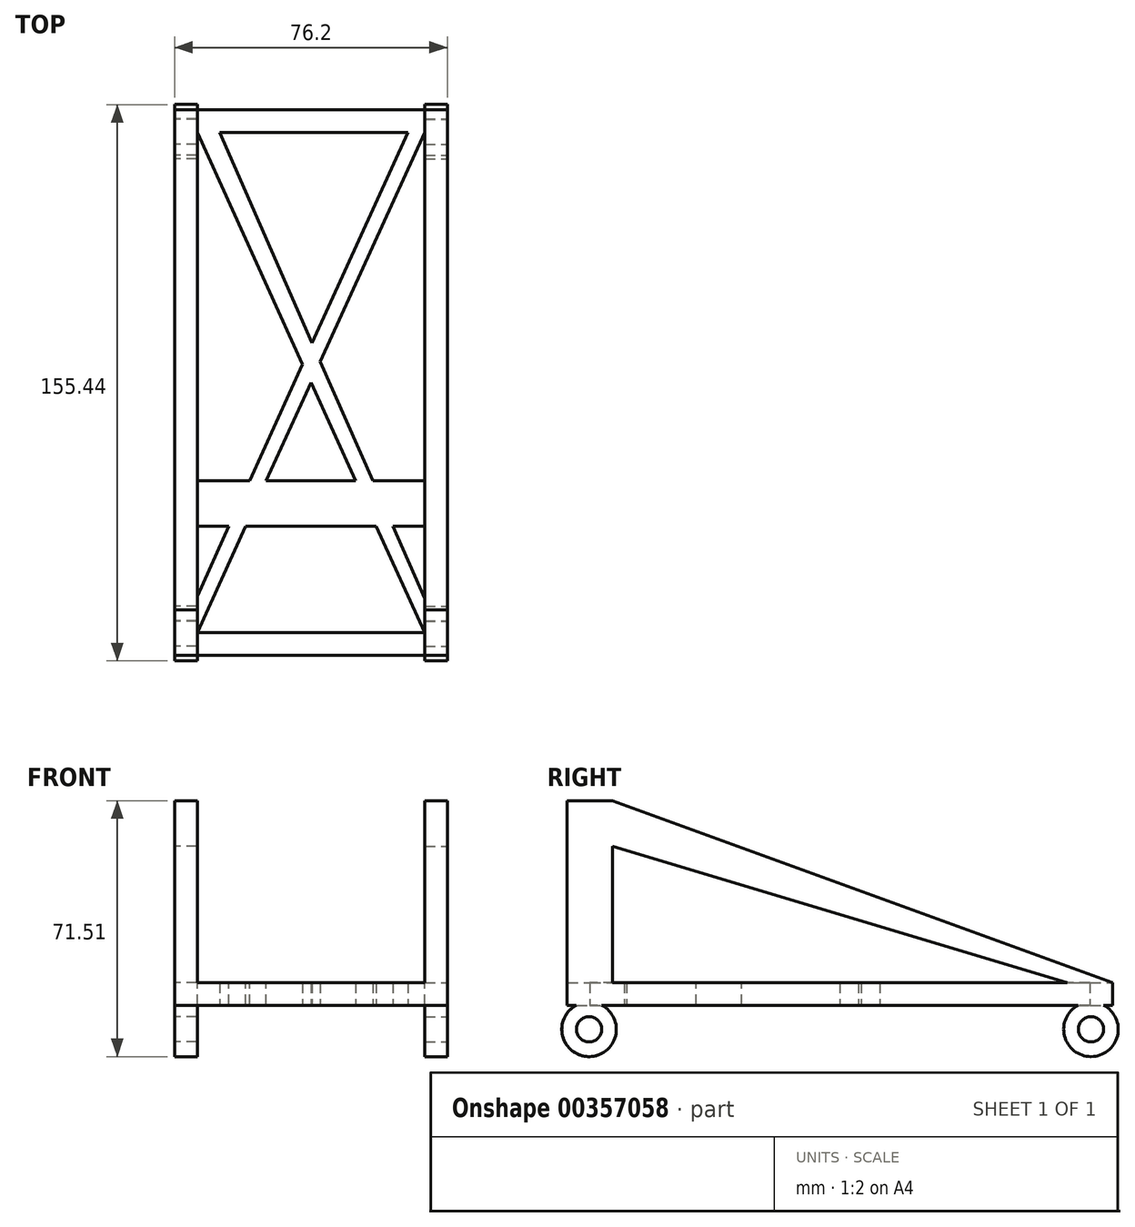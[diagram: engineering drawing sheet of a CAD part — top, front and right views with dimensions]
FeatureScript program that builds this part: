
annotation { "Feature Type Name" : "Feature", "Feature Type Description" : "" }
export const myFeature = defineFeature(function(context is Context, id is Id, definition is map)
    precondition{}
    {
        {
            var Q0;
            Q0=qCreatedBy(makeId("Top.planeOp"),FACE);
            var sketch = newSketch(context, id + "F0", { "sketchPlane" : qUnion([Q0])});
            skLineSegment(sketch, "E0.bottom", {"start": v(-38.1, -76.2) * mm, "end": v(38.1, -76.2) * mm});
            skLineSegment(sketch, "E0.top", {"start": v(-38.1, 76.2) * mm, "end": v(38.1, 76.2) * mm});
            skLineSegment(sketch, "E0.left", {"start": v(-38.1, -76.2) * mm, "end": v(-38.1, 76.2) * mm});
            skLineSegment(sketch, "E0.right", {"start": v(38.1, -76.2) * mm, "end": v(38.1, 76.2) * mm});
            skPoint(sketch, "E0.middle", {"position": v(0, 0) * mm});
            skLineSegment(sketch, "E1.bottom", {"start": v(-31.75, 69.85) * mm, "end": v(31.75, 69.85) * mm});
            skLineSegment(sketch, "E1.top", {"start": v(-31.75, -69.85) * mm, "end": v(31.75, -69.85) * mm});
            skLineSegment(sketch, "E1.left", {"start": v(-31.75, 69.85) * mm, "end": v(-31.75, -69.85) * mm});
            skLineSegment(sketch, "E1.right", {"start": v(31.75, 69.85) * mm, "end": v(31.75, -69.85) * mm});
            skLineSegment(sketch, "E2", {"start": v(-31.75, -59.6) * mm, "end": v(27.09, 69.85) * mm});
            skLineSegment(sketch, "E3", {"start": v(-31.75, -69.85) * mm, "end": v(31.75, 69.85) * mm});
            skLineSegment(sketch, "E4", {"start": v(-25.47, 69.85) * mm, "end": v(31.75, -60.32) * mm});
            skLineSegment(sketch, "E5", {"start": v(-31.75, 69.85) * mm, "end": v(31.75, -69.85) * mm});
            skSolve(sketch);
        }
        {
            var Q0;
            Q0=qSketchRegion(id+"F0",true);
            var Q1;
            {var subQ0=sQuery(id+"F0.wireOp",EDGE,"E5");var subQ5=sQuery(id+"F0.wireOp",EDGE,"E2");var subQ6=makeQuery(id+"F0.imprint","INTERSECT",VERTEX,{"derivedFrom":[subQ5,subQ0]});Q1=makeQuery(id+"F0.imprint","IMPRINT",FACE,{"disambiguationData":[TD([[makeQuery(id+"F0.imprint","IMPRINT",EDGE,{"disambiguationData":[TD([[subQ6,-1.0]])],"derivedFrom":subQ5}),1.0]])]});}
            var Q2;
            {var subQ1=sQuery(id+"F0.wireOp",EDGE,"E1.bottom");var subQ3=sQuery(id+"F0.wireOp",EDGE,"E2");var subQ4=makeQuery(id+"F0.imprint","INTERSECT",VERTEX,{"derivedFrom":[subQ1,subQ3]});Q2=makeQuery(id+"F0.imprint","IMPRINT",FACE,{"disambiguationData":[TD([[makeQuery(id+"F0.imprint","IMPRINT",EDGE,{"disambiguationData":[TD([[subQ4,1.0]])],"derivedFrom":subQ3}),-1.0]])]});}
            var Q3;
            {var subQ0=sQuery(id+"F0.wireOp",EDGE,"E5");var subQ5=sQuery(id+"F0.wireOp",EDGE,"E3");var subQ6=makeQuery(id+"F0.imprint","INTERSECT",VERTEX,{"derivedFrom":[subQ5,subQ0]});Q3=makeQuery(id+"F0.imprint","IMPRINT",FACE,{"disambiguationData":[TD([[makeQuery(id+"F0.imprint","IMPRINT",EDGE,{"disambiguationData":[TD([[subQ6,-1.0]])],"derivedFrom":subQ5}),-1.0]])]});}
            var Q4;
            {var subQ1=sQuery(id+"F0.wireOp",EDGE,"E1.left");var subQ3=sQuery(id+"F0.wireOp",EDGE,"E2");var subQ4=makeQuery(id+"F0.imprint","INTERSECT",VERTEX,{"derivedFrom":[subQ1,subQ3]});Q4=makeQuery(id+"F0.imprint","IMPRINT",FACE,{"disambiguationData":[TD([[makeQuery(id+"F0.imprint","IMPRINT",EDGE,{"disambiguationData":[TD([[subQ4,-1.0]])],"derivedFrom":subQ3}),-1.0]])]});}
            var Q5;
            {var subQ0=sQuery(id+"F0.wireOp",EDGE,"E5");var subQ1=sQuery(id+"F0.wireOp",EDGE,"E2");var subQ2=makeQuery(id+"F0.imprint","INTERSECT",VERTEX,{"derivedFrom":[subQ1,subQ0]});Q5=makeQuery(id+"F0.imprint","IMPRINT",FACE,{"disambiguationData":[TD([[makeQuery(id+"F0.imprint","IMPRINT",EDGE,{"disambiguationData":[TD([[subQ2,-1.0]])],"derivedFrom":subQ1}),-1.0]])]});}
            extrude(context, id + "F1", {"entities" : qUnion([Q0, Q1, Q2, Q3, Q4, Q5]), "endBound" : BoundingType.SYMMETRIC, "depth" : 6.35 * mm});
        }
        {
            var Q0;
            Q0=makeQuery(id+"F1.opExtrude","SWEPT_FACE",FACE,{"disambiguationData":[OSD([sQuery(id+"F0.wireOp",EDGE,"E0.right")])]});
            var sketch = newSketch(context, id + "F2", { "sketchPlane" : qUnion([Q0])});
            skLineSegment(sketch, "E6.bottom", {"start": v(-76.2, 3.18) * mm, "end": v(-63.5, 3.18) * mm});
            skLineSegment(sketch, "E6.top", {"start": v(-76.2, 53.98) * mm, "end": v(-63.5, 53.98) * mm});
            skLineSegment(sketch, "E6.left", {"start": v(-76.2, 3.17) * mm, "end": v(-76.2, 53.98) * mm});
            skLineSegment(sketch, "E6.right", {"start": v(-63.5, 3.17) * mm, "end": v(-63.5, 53.98) * mm});
            skLineSegment(sketch, "E7", {"start": v(-63.5, 53.98) * mm, "end": v(76.2, 3.17) * mm});
            skLineSegment(sketch, "E8", {"start": v(-63.5, 41.27) * mm, "end": v(63.5, 3.18) * mm});
            skSolve(sketch);
        }
        {
            var Q0;
            Q0=qSketchRegion(id+"F2",true);
            var Q1;
            {var subQ0=sQuery(id+"F2.wireOp",EDGE,"E7");Q1=makeQuery(id+"F2.imprint","IMPRINT",FACE,{"disambiguationData":[TD([[makeQuery(id+"F2.imprint","IMPRINT",EDGE,{"derivedFrom":subQ0}),-1.0]])]});}
            extrude(context, id + "F3", {"entities" : qUnion([Q0, Q1]), "operationType" : NewBodyOperationType.ADD, "oppositeDirection" : true, "depth" : 6.35 * mm});
        }
        {
            var Q0;
            Q0=makeQuery(id+"F1.opExtrude","SWEPT_FACE",FACE,{"disambiguationData":[OSD([sQuery(id+"F0.wireOp",EDGE,"E0.left")])]});
            var sketch = newSketch(context, id + "F4", { "sketchPlane" : qUnion([Q0])});
            skLineSegment(sketch, "E9.bottom", {"start": v(76.2, 3.18) * mm, "end": v(63.5, 3.17) * mm});
            skLineSegment(sketch, "E9.top", {"start": v(76.2, 53.97) * mm, "end": v(63.5, 53.97) * mm});
            skLineSegment(sketch, "E9.left", {"start": v(76.2, 3.17) * mm, "end": v(76.2, 53.97) * mm});
            skLineSegment(sketch, "E9.right", {"start": v(63.5, 3.17) * mm, "end": v(63.5, 53.97) * mm});
            skLineSegment(sketch, "E10", {"start": v(63.5, 53.97) * mm, "end": v(-76.2, 3.17) * mm});
            skLineSegment(sketch, "E11", {"start": v(63.5, 41.28) * mm, "end": v(-63.5, 3.17) * mm});
            skSolve(sketch);
        }
        {
            var Q0;
            Q0=qSketchRegion(id+"F4",true);
            var Q1;
            {var subQ0=sQuery(id+"F4.wireOp",EDGE,"E10");Q1=makeQuery(id+"F4.imprint","IMPRINT",FACE,{"disambiguationData":[TD([[makeQuery(id+"F4.imprint","IMPRINT",EDGE,{"derivedFrom":subQ0}),1.0]])]});}
            extrude(context, id + "F5", {"entities" : qUnion([Q0, Q1]), "operationType" : NewBodyOperationType.ADD, "oppositeDirection" : true, "depth" : 6.35 * mm});
        }
        {
            var Q0;
            {var subQ0=sQuery(id+"F0.wireOp",EDGE,"E0.right");Q0=makeQuery(id+"F3.boolean.opBoolean","MERGE",FACE,{"derivedFrom":[makeQuery(id+"F1.opExtrude","SWEPT_FACE",FACE,{"disambiguationData":[OSD([subQ0])]}),makeQuery(id+"F3.opExtrude","CAP_FACE",FACE,{"disambiguationData":[OSD([subQ0,sQuery(id+"F2.wireOp",EDGE,"E6.bottom"),sQuery(id+"F2.wireOp",EDGE,"E6.top"),sQuery(id+"F2.wireOp",EDGE,"E6.left"),sQuery(id+"F2.wireOp",EDGE,"E6.right"),sQuery(id+"F2.wireOp",EDGE,"E7"),sQuery(id+"F2.wireOp",EDGE,"E8")])],"isStart":true})]});}
            var sketch = newSketch(context, id + "F6", { "sketchPlane" : qUnion([Q0])});
            skArc(sketch, "E12", {"start": v(-73.66, -3.18) * mm, "mid": v(-70.1, -17.53) * mm, "end": v(-66.54, -3.18) * mm});
            skCircle(sketch, "E13", {"center": v(-70.1, -9.91) * mm, "radius": 3.53 * mm});
            skArc(sketch, "E14", {"start": v(66.55, -3.18) * mm, "mid": v(70.1, -17.53) * mm, "end": v(73.66, -3.18) * mm});
            skCircle(sketch, "E15", {"center": v(70.1, -9.91) * mm, "radius": 3.53 * mm});
            skSolve(sketch);
        }
        {
            var Q0;
            {var subQ0=sQuery(id+"F6.wireOp",EDGE,"E12");Q0=makeQuery(id+"F6.imprint","IMPRINT",FACE,{"disambiguationData":[TD([[makeQuery(id+"F6.imprint","IMPRINT",EDGE,{"derivedFrom":subQ0}),1.0]])]});}
            var Q1;
            {var subQ0=sQuery(id+"F6.wireOp",EDGE,"E14");Q1=makeQuery(id+"F6.imprint","IMPRINT",FACE,{"disambiguationData":[TD([[makeQuery(id+"F6.imprint","IMPRINT",EDGE,{"derivedFrom":subQ0}),1.0]])]});}
            extrude(context, id + "F7", {"entities" : qUnion([Q0, Q1]), "operationType" : NewBodyOperationType.ADD, "oppositeDirection" : true, "depth" : 6.35 * mm});
        }
        {
            var Q0;
            {var subQ0=sQuery(id+"F0.wireOp",EDGE,"E0.left");Q0=makeQuery(id+"F5.boolean.opBoolean","MERGE",FACE,{"derivedFrom":[makeQuery(id+"F1.opExtrude","SWEPT_FACE",FACE,{"disambiguationData":[OSD([subQ0])]}),makeQuery(id+"F5.opExtrude","CAP_FACE",FACE,{"disambiguationData":[OSD([subQ0,sQuery(id+"F4.wireOp",EDGE,"E9.bottom"),sQuery(id+"F4.wireOp",EDGE,"E9.top"),sQuery(id+"F4.wireOp",EDGE,"E9.left"),sQuery(id+"F4.wireOp",EDGE,"E9.right"),sQuery(id+"F4.wireOp",EDGE,"E10"),sQuery(id+"F4.wireOp",EDGE,"E11")])],"isStart":true})]});}
            var sketch = newSketch(context, id + "F8", { "sketchPlane" : qUnion([Q0])});
            skArc(sketch, "E16", {"start": v(-73.66, -3.17) * mm, "mid": v(-70.1, -17.53) * mm, "end": v(-66.55, -3.17) * mm});
            skArc(sketch, "E17", {"start": v(66.55, -3.18) * mm, "mid": v(70.1, -17.53) * mm, "end": v(73.66, -3.18) * mm});
            skCircle(sketch, "E18", {"center": v(-70.1, -9.91) * mm, "radius": 3.53 * mm});
            skCircle(sketch, "E19", {"center": v(70.1, -9.91) * mm, "radius": 3.53 * mm});
            skSolve(sketch);
        }
        {
            var Q0;
            {var subQ0=sQuery(id+"F8.wireOp",EDGE,"E16");Q0=makeQuery(id+"F8.imprint","IMPRINT",FACE,{"disambiguationData":[TD([[makeQuery(id+"F8.imprint","IMPRINT",EDGE,{"derivedFrom":subQ0}),1.0]])]});}
            var Q1;
            {var subQ0=sQuery(id+"F8.wireOp",EDGE,"E17");Q1=makeQuery(id+"F8.imprint","IMPRINT",FACE,{"disambiguationData":[TD([[makeQuery(id+"F8.imprint","IMPRINT",EDGE,{"derivedFrom":subQ0}),1.0]])]});}
            extrude(context, id + "F9", {"entities" : qUnion([Q0, Q1]), "operationType" : NewBodyOperationType.ADD, "oppositeDirection" : true, "depth" : 6.35 * mm});
        }
        {
            var Q0;
            {var subQ6=sQuery(id+"F0.wireOp",EDGE,"E0.left");var subQ8=sQuery(id+"F0.wireOp",EDGE,"E5");var subQ9=sQuery(id+"F0.wireOp",EDGE,"E1.right");var subQ10=sQuery(id+"F0.wireOp",EDGE,"E1.top");var subQ11=sQuery(id+"F0.wireOp",EDGE,"E3");var subQ13=sQuery(id+"F0.wireOp",EDGE,"E1.left");var subQ14=sQuery(id+"F0.wireOp",EDGE,"E1.bottom");var subQ15=sQuery(id+"F0.wireOp",EDGE,"E2");var subQ17=sQuery(id+"F0.wireOp",EDGE,"E4");var subQ25=sQuery(id+"F0.wireOp",EDGE,"E0.right");var subQ26=sQuery(id+"F0.wireOp",EDGE,"E0.top");var subQ27=makeQuery(id+"F1.opExtrude","CAP_FACE",FACE,{"disambiguationData":[OSD([sQuery(id+"F0.wireOp",EDGE,"E0.bottom"),subQ26,subQ6,subQ25,subQ14,subQ10,subQ13,subQ9,subQ15,subQ11,subQ17,subQ8])],"isStart":false});Q0=makeQuery(id+"F5.boolean.opBoolean","SPLIT",FACE,{"disambiguationData":[TD([makeQuery(id+"F1.opExtrude","SWEPT_FACE",FACE,{"disambiguationData":[OSD([subQ26])]})])],"derivedFrom":subQ27});}
            var sketch = newSketch(context, id + "F10", { "sketchPlane" : qUnion([Q0])});
            skLineSegment(sketch, "E20.bottom", {"start": v(-31.75, -27.43) * mm, "end": v(31.75, -27.43) * mm});
            skLineSegment(sketch, "E20.top", {"start": v(-31.75, -40.13) * mm, "end": v(31.75, -40.13) * mm});
            skLineSegment(sketch, "E20.left", {"start": v(-31.75, -27.43) * mm, "end": v(-31.75, -40.13) * mm});
            skLineSegment(sketch, "E20.right", {"start": v(31.75, -27.43) * mm, "end": v(31.75, -40.13) * mm});
            skSolve(sketch);
        }
        {
            var Q0;
            Q0=qSketchRegion(id+"F10",true);
            extrude(context, id + "F11", {"entities" : qUnion([Q0]), "operationType" : NewBodyOperationType.ADD, "oppositeDirection" : true, "depth" : 6.35 * mm});
        }
        {
            var Q0;
            Q0=makeQuery(id+"F1.opExtrude","SWEPT_BODY",BODY,{"disambiguationData":[OSD([sQuery(id+"F0.wireOp",EDGE,"E0.bottom"),sQuery(id+"F0.wireOp",EDGE,"E0.top"),sQuery(id+"F0.wireOp",EDGE,"E0.left"),sQuery(id+"F0.wireOp",EDGE,"E0.right"),sQuery(id+"F0.wireOp",EDGE,"E1.bottom"),sQuery(id+"F0.wireOp",EDGE,"E1.top"),sQuery(id+"F0.wireOp",EDGE,"E1.left"),sQuery(id+"F0.wireOp",EDGE,"E1.right"),sQuery(id+"F0.wireOp",EDGE,"E2"),sQuery(id+"F0.wireOp",EDGE,"E3"),sQuery(id+"F0.wireOp",EDGE,"E4"),sQuery(id+"F0.wireOp",EDGE,"E5")])]});
            transform(context, id + "F12", {"entities" : qUnion([Q0]), "transformType" : TransformType.TRANSLATION_3D, "dx" : 0 * mm, "dy" : 0 * mm, "dz" : 0 * mm, "makeCopy" : true});
        }
    });
